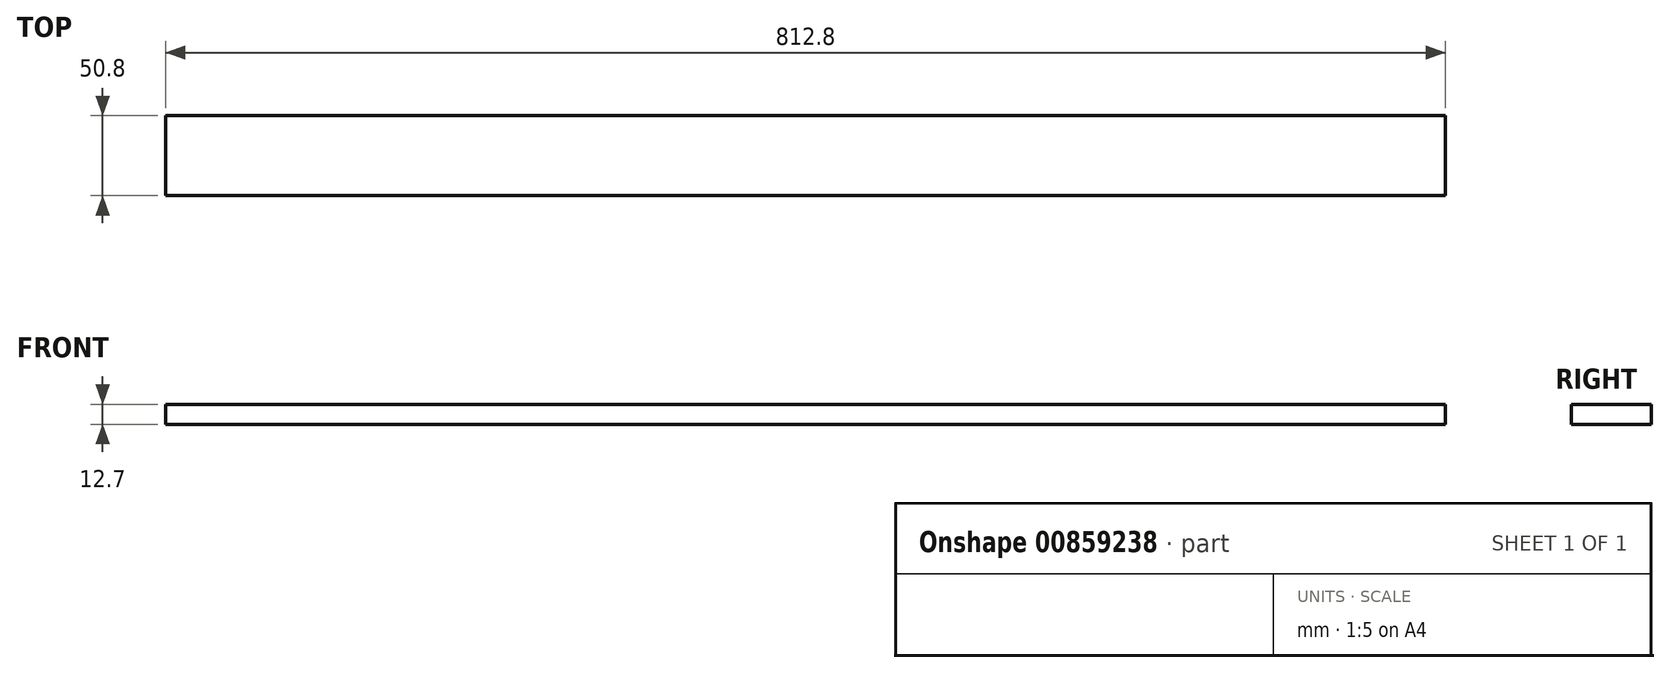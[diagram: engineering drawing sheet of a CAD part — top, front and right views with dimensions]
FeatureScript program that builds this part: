
annotation { "Feature Type Name" : "Feature", "Feature Type Description" : "" }
export const myFeature = defineFeature(function(context is Context, id is Id, definition is map)
    precondition{}
    {
        {
            var Q0;
            Q0=qCreatedBy(makeId("Top.planeOp"),FACE);
            var sketch = newSketch(context, id + "F0", { "sketchPlane" : qUnion([Q0])});
            skLineSegment(sketch, "E0.bottom", {"start": v(0, 0) * mm, "end": v(-812.8, 0) * mm});
            skLineSegment(sketch, "E0.top", {"start": v(0, 50.8) * mm, "end": v(-812.8, 50.8) * mm});
            skLineSegment(sketch, "E0.left", {"start": v(0, 0) * mm, "end": v(0, 50.8) * mm});
            skLineSegment(sketch, "E0.right", {"start": v(-812.8, 0) * mm, "end": v(-812.8, 50.8) * mm});
            skSolve(sketch);
        }
        {
            var Q0;
            Q0=makeQuery(id+"F0.imprint","IMPRINT",FACE,{"disambiguationData":[TD([[makeQuery(id+"F0.imprint","IMPRINT",EDGE,{"derivedFrom":sQuery(id+"F0.wireOp",EDGE,"E0.bottom")}),-1.0]])]});
            extrude(context, id + "F1", {"entities" : qUnion([Q0]), "depth" : 12.7 * mm, "offsetDistance" : 25.4 * mm});
        }
    });
